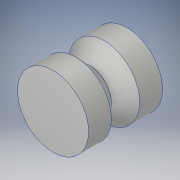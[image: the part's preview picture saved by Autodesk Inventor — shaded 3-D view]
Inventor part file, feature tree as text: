
AUTODESK INVENTOR PART (.ipt)
format: ipt  version: 2019 (Build 230136000, 136)  size: 113,152 bytes
history: native  units: in
note: dims shown in document units (in); Inventor stores cm internally (conversion verified against a paired STEP export)
features: extrude x2, chamfer x2, sketch x2
ambient origin geometry x8: Origin, YZ Plane, XZ Plane, XY Plane, X Axis, Y Axis, Z Axis, Center Point
bodies: Solid1 (feature_tree)
feature tree (6):
  extrude  "Extrusion1"  Depth=0.26in TaperAngle=0.0deg
  chamfer  "Chamfer1"  Distance=0.1in Angle=45.0deg
  extrude  "Extrusion2"  Depth=0.26in TaperAngle=0.0deg
  chamfer  "Chamfer2"  Distance=0.1in Angle=45.0deg
  sketch  "Sketch1"  dims[d0=0.5in d1=0.26in d2=0.0in d3=0.1in d4=0.125in d5=45.0deg]
  sketch  "Sketch2"  dims[d6=0.5in d7=0.26in d8=0.0in d9=0.1in d10=0.125in d11=45.0deg]
